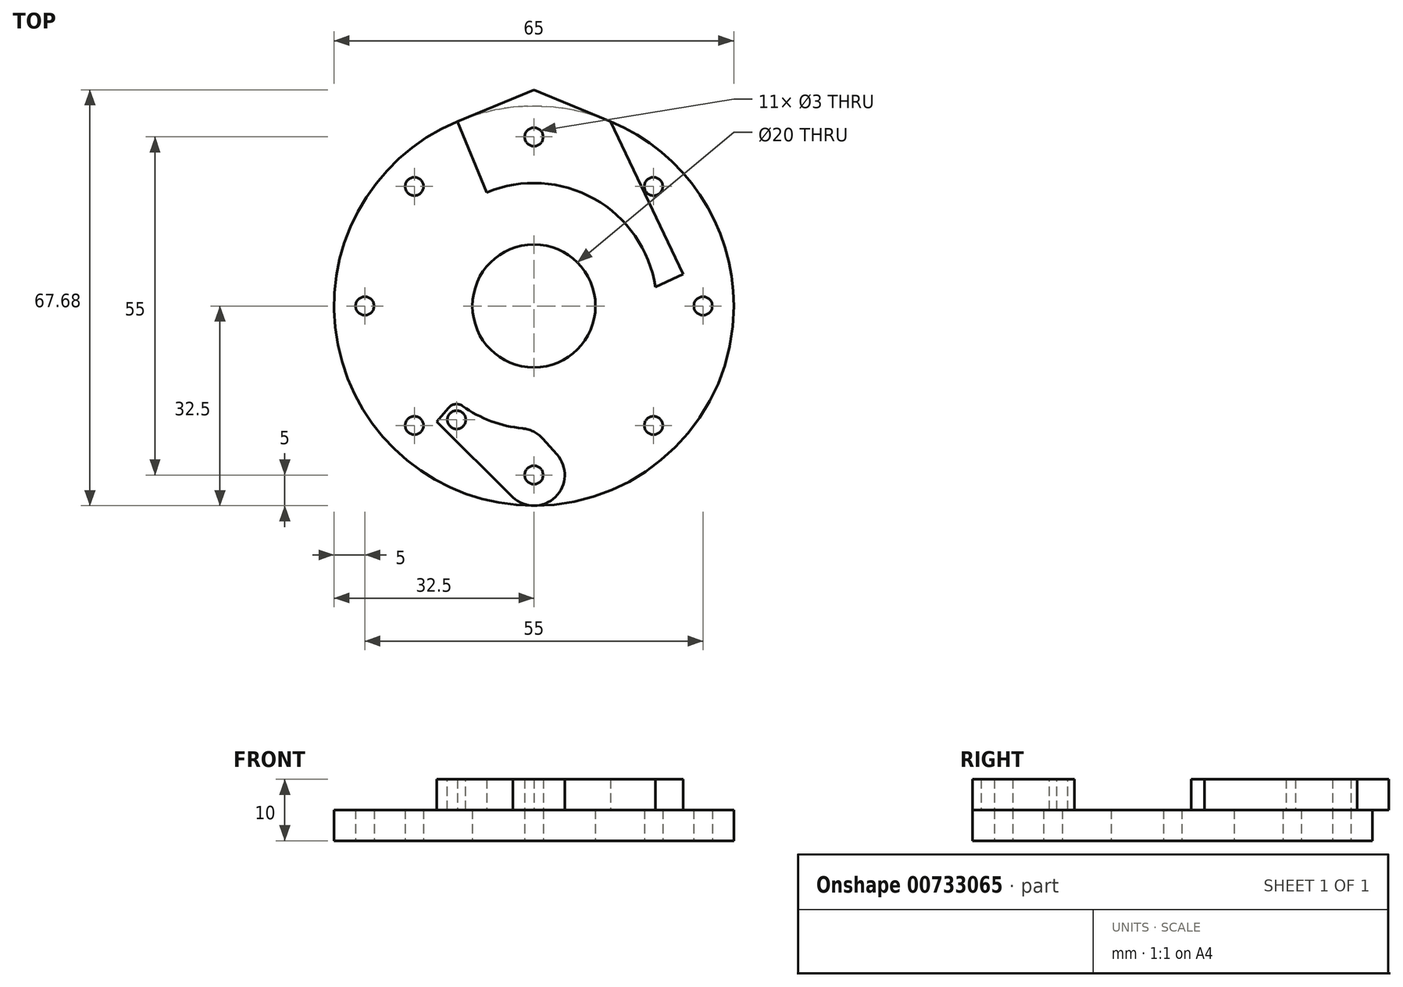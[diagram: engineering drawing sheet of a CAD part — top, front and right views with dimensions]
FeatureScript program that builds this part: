
annotation { "Feature Type Name" : "Feature", "Feature Type Description" : "" }
export const myFeature = defineFeature(function(context is Context, id is Id, definition is map)
    precondition{}
    {
        {
            var Q0;
            Q0=qCreatedBy(makeId("Top.planeOp"),FACE);
            var sketch = newSketch(context, id + "F0", { "sketchPlane" : qUnion([Q0])});
            skCircle(sketch, "E0", {"center": v(0, 0) * mm, "radius": 32.5 * mm});
            skCircle(sketch, "E1", {"center": v(0, 27.5) * mm, "radius": 1.5 * mm});
            skPoint(sketch, "E2", {"position": v(0, 32.5) * mm});
            skCircle(sketch, "E3.1.0", {"center": v(-19.45, 19.45) * mm, "radius": 1.5 * mm});
            skCircle(sketch, "E3.2.0", {"center": v(-27.5, 0) * mm, "radius": 1.5 * mm});
            skCircle(sketch, "E3.3.0", {"center": v(-19.45, -19.45) * mm, "radius": 1.5 * mm});
            skCircle(sketch, "E3.4.0", {"center": v(0, -27.5) * mm, "radius": 1.5 * mm});
            skCircle(sketch, "E3.5.0", {"center": v(19.45, -19.45) * mm, "radius": 1.5 * mm});
            skCircle(sketch, "E3.6.0", {"center": v(27.5, 0) * mm, "radius": 1.5 * mm});
            skCircle(sketch, "E3.7.0", {"center": v(19.45, 19.45) * mm, "radius": 1.5 * mm});
            skCircle(sketch, "E4", {"center": v(0, 0) * mm, "radius": 10 * mm});
            skSolve(sketch);
        }
        {
            var Q0;
            Q0=qSketchRegion(id+"F0",true);
            extrude(context, id + "F1", {"entities" : qUnion([Q0]), "depth" : 5 * mm, "offsetDistance" : 25 * mm});
        }
        {
            var Q0;
            Q0=makeQuery(id+"F1.opExtrude","CAP_FACE",FACE,{"disambiguationData":[OSD([sQuery(id+"F0.wireOp",EDGE,"E0"),sQuery(id+"F0.wireOp",EDGE,"E1"),sQuery(id+"F0.wireOp",EDGE,"E3.1.0"),sQuery(id+"F0.wireOp",EDGE,"E3.2.0"),sQuery(id+"F0.wireOp",EDGE,"E3.3.0"),sQuery(id+"F0.wireOp",EDGE,"E3.4.0"),sQuery(id+"F0.wireOp",EDGE,"E3.5.0"),sQuery(id+"F0.wireOp",EDGE,"E3.6.0"),sQuery(id+"F0.wireOp",EDGE,"E3.7.0")])],"isStart":false});
            var sketch = newSketch(context, id + "F2", { "sketchPlane" : qUnion([Q0])});
            skCircle(sketch, "E5.0", {"center": v(0, 0) * mm, "radius": 32.5 * mm, "construction": true});
            skLineSegment(sketch, "E6.0", {"start": v(0, 35.18) * mm, "end": v(24.87, 24.87) * mm});
            skLineSegment(sketch, "E6.1", {"start": v(24.87, 24.87) * mm, "end": v(35.18, 0) * mm});
            skLineSegment(sketch, "E6.2", {"start": v(35.18, 0) * mm, "end": v(24.87, -24.87) * mm});
            skLineSegment(sketch, "E6.3", {"start": v(24.87, -24.87) * mm, "end": v(0, -35.18) * mm});
            skLineSegment(sketch, "E6.4", {"start": v(0, -35.18) * mm, "end": v(-24.87, -24.87) * mm});
            skLineSegment(sketch, "E6.5", {"start": v(-24.87, -24.87) * mm, "end": v(-35.18, 0) * mm});
            skLineSegment(sketch, "E6.6", {"start": v(-35.18, 0) * mm, "end": v(-24.87, 24.87) * mm});
            skLineSegment(sketch, "E6.7", {"start": v(-24.87, 24.87) * mm, "end": v(0, 35.18) * mm});
            skPoint(sketch, "E6.0.midPoint", {"position": v(12.44, 30.03) * mm});
            skCircle(sketch, "E7", {"center": v(0, 0) * mm, "radius": 20 * mm});
            skPoint(sketch, "E8", {"position": v(-12.44, 30.03) * mm});
            skLineSegment(sketch, "E9", {"start": v(-12.44, 30.03) * mm, "end": v(-7.65, 18.48) * mm});
            skLineSegment(sketch, "E10.MirrorCS", {"start": v(12.44, 30.03) * mm, "end": v(7.65, 18.48) * mm, "construction": true});
            skCircle(sketch, "E11.0", {"center": v(0, 27.5) * mm, "radius": 1.5 * mm});
            skLineSegment(sketch, "E12", {"start": v(12.44, 30.03) * mm, "end": v(24.28, 5.2) * mm});
            skLineSegment(sketch, "E13", {"start": v(24.28, 5.2) * mm, "end": v(19.77, 3.05) * mm});
            skArc(sketch, "E14.trimOffspring", {"start": v(-16.07, -19.15) * mm, "mid": v(-10.46, -22.7) * mm, "end": v(-4.11, -24.66) * mm});
            skLineSegment(sketch, "E15", {"start": v(-16.07, -19.15) * mm, "end": v(-12.86, -15.32) * mm});
            skCircle(sketch, "E16", {"center": v(0, -27.5) * mm, "radius": 5 * mm});
            skLineSegment(sketch, "E17", {"start": v(0, -22.5) * mm, "end": v(0, -20) * mm});
            skLineSegment(sketch, "E18", {"start": v(-17.16, -18.18) * mm, "end": v(-3.43, -31.14) * mm});
            skLineSegment(sketch, "E19", {"start": v(0, -20) * mm, "end": v(3.73, -24.17) * mm});
            skLineSegment(sketch, "E20", {"start": v(-16.07, -19.15) * mm, "end": v(-16.1, -19.18) * mm});
            skSolve(sketch);
        }
        {
            var Q0;
            Q0=makeQuery(id+"F2.imprint","IMPRINT",FACE,{"disambiguationData":[TD([[makeQuery(id+"F2.imprint","IMPRINT",EDGE,{"derivedFrom":makeQuery(id+"F1.opExtrude","CAP_EDGE",EDGE,{"disambiguationData":[OSD([sQuery(id+"F0.wireOp",EDGE,"E3.4.0")])],"isStart":false})}),-1.0]])]});
            var Q1;
            {var subQ0=sQuery(id+"F2.wireOp",EDGE,"E15");var subQ1=sQuery(id+"F2.wireOp",EDGE,"E14.trimOffspring");var subQ2=makeQuery(id+"F2.imprint","INTERSECT",VERTEX,{"derivedFrom":[subQ1,subQ0]});Q1=makeQuery(id+"F2.imprint","IMPRINT",FACE,{"disambiguationData":[TD([[makeQuery(id+"F2.imprint","IMPRINT",EDGE,{"disambiguationData":[TD([[subQ2,-1.0]])],"derivedFrom":subQ1}),1.0]])]});}
            var Q2;
            {var subQ0=sQuery(id+"F2.wireOp",EDGE,"E14.trimOffspring");var subQ1=makeQuery(id+"F1.opExtrude","CAP_EDGE",EDGE,{"disambiguationData":[OSD([sQuery(id+"F0.wireOp",EDGE,"E3.3.0")])],"isStart":false});var subQ2=makeQuery(id+"F2.imprint","INTERSECT",VERTEX,{"disambiguationData":[OD(0.0)],"derivedFrom":[subQ1,subQ0]});Q2=makeQuery(id+"F2.imprint","IMPRINT",FACE,{"disambiguationData":[TD([[makeQuery(id+"F2.imprint","IMPRINT",EDGE,{"disambiguationData":[TD([[subQ2,-1.0]])],"derivedFrom":subQ0}),1.0]])]});}
            var Q3;
            {var subQ3=sQuery(id+"F2.wireOp",EDGE,"TiWqFANf-cDh7-nF8t-lKnd-fGeFsKGwED6M");Q3=makeQuery(id+"F2.imprint","IMPRINT",FACE,{"disambiguationData":[TD([[makeQuery(id+"F2.imprint","IMPRINT",EDGE,{"derivedFrom":subQ3}),1.0]])]});}
            var Q4;
            {var subQ6=sQuery(id+"F2.wireOp",EDGE,"E9");Q4=makeQuery(id+"F2.imprint","IMPRINT",FACE,{"disambiguationData":[TD([[makeQuery(id+"F2.imprint","IMPRINT",EDGE,{"derivedFrom":subQ6}),1.0]])]});}
            var Q5;
            {var subQ0=sQuery(id+"F2.wireOp",EDGE,"E12");var subQ1=makeQuery(id+"F1.opExtrude","CAP_EDGE",EDGE,{"disambiguationData":[OSD([sQuery(id+"F0.wireOp",EDGE,"E3.7.0")])],"isStart":false});var subQ2=makeQuery(id+"F2.imprint","INTERSECT",VERTEX,{"disambiguationData":[OD(0.0)],"derivedFrom":[subQ1,subQ0]});Q5=makeQuery(id+"F2.imprint","IMPRINT",FACE,{"disambiguationData":[TD([[makeQuery(id+"F2.imprint","IMPRINT",EDGE,{"disambiguationData":[TD([[subQ2,-1.0]])],"derivedFrom":subQ0}),-1.0]])]});}
            var Q6;
            {var subQ0=sQuery(id+"F2.wireOp",EDGE,"E6.7");var subQ1=sQuery(id+"F2.wireOp",EDGE,"E6.0");var subQ2=makeQuery(id+"F2.imprint","INTERSECT",VERTEX,{"derivedFrom":[subQ1,subQ0]});Q6=makeQuery(id+"F2.imprint","IMPRINT",FACE,{"disambiguationData":[TD([[makeQuery(id+"F2.imprint","IMPRINT",EDGE,{"disambiguationData":[TD([[subQ2,-1.0]])],"derivedFrom":subQ1}),-1.0]])]});}
            var Q7;
            {var subQ0=sQuery(id+"F2.wireOp",EDGE,"E17");Q7=makeQuery(id+"F2.imprint","IMPRINT",FACE,{"disambiguationData":[TD([[makeQuery(id+"F2.imprint","IMPRINT",EDGE,{"derivedFrom":subQ0}),-1.0]])]});}
            var Q8;
            {var subQ3=sQuery(id+"F2.wireOp",EDGE,"E18");Q8=makeQuery(id+"F2.imprint","IMPRINT",FACE,{"disambiguationData":[TD([[makeQuery(id+"F2.imprint","IMPRINT",EDGE,{"derivedFrom":subQ3}),1.0]])]});}
            extrude(context, id + "F3", {"entities" : qUnion([Q0, Q1, Q2, Q3, Q4, Q5, Q6, Q7, Q8]), "depth" : 5 * mm, "offsetDistance" : 25 * mm});
        }
        {
            var Q0;
            Q0=makeQuery(id+"F3.opExtrude","CAP_FACE",FACE,{"disambiguationData":[OSD([sQuery(id+"F0.wireOp",EDGE,"E3.4.0"),sQuery(id+"F2.wireOp",EDGE,"E7"),sQuery(id+"F2.wireOp",EDGE,"E15"),sQuery(id+"F2.wireOp",EDGE,"E16"),sQuery(id+"F2.wireOp",EDGE,"E18"),sQuery(id+"F2.wireOp",EDGE,"E19"),sQuery(id+"F2.wireOp",EDGE,"E20")])],"isStart":false});
            var sketch = newSketch(context, id + "F4", { "sketchPlane" : qUnion([Q0])});
            skLineSegment(sketch, "E21", {"start": v(-15.78, -18.8) * mm, "end": v(-3.43, -31.14) * mm});
            skLineSegment(sketch, "E22", {"start": v(-15.78, -18.8) * mm, "end": v(-12.3, -21.72) * mm, "construction": true});
            skLineSegment(sketch, "E23", {"start": v(-12.86, -15.32) * mm, "end": v(-9.38, -18.24) * mm, "construction": true});
            skLineSegment(sketch, "E24", {"start": v(-12.3, -21.72) * mm, "end": v(-9.38, -18.24) * mm, "construction": true});
            skLineSegment(sketch, "E25", {"start": v(-10.84, -19.98) * mm, "end": v(-14.32, -17.06) * mm, "construction": true});
            skCircle(sketch, "E26", {"center": v(-12.58, -18.52) * mm, "radius": 1.5 * mm});
            skSolve(sketch);
        }
        {
            var Q0;
            {var subQ0=sQuery(id+"F4.wireOp",EDGE,"E21");Q0=makeQuery(id+"F4.imprint","IMPRINT",FACE,{"disambiguationData":[TD([[makeQuery(id+"F4.imprint","IMPRINT",EDGE,{"derivedFrom":subQ0}),-1.0]])]});}
            var Q1;
            Q1=makeQuery(id+"F4.imprint","IMPRINT",FACE,{"disambiguationData":[TD([[makeQuery(id+"F4.imprint","IMPRINT",EDGE,{"derivedFrom":sQuery(id+"F4.wireOp",EDGE,"E26")}),1.0]])]});
            extrude(context, id + "F5", {"entities" : qUnion([Q0, Q1]), "operationType" : NewBodyOperationType.REMOVE, "endBound" : BoundingType.UP_TO_NEXT, "oppositeDirection" : true, "depth" : 25 * mm, "offsetDistance" : 25 * mm});
        }
        {
            var Q0;
            Q0=makeQuery(id+"F5.boolean.opBoolean","COPY",EDGE,{"derivedFrom":makeQuery(id+"F5.opExtrude","SWEPT_EDGE",EDGE,{"disambiguationData":[OSD([sQuery(id+"F2.wireOp",EDGE,"E15"),sQuery(id+"F2.wireOp",EDGE,"E20"),sQuery(id+"F4.wireOp",EDGE,"E21")])]})});
            var Q1;
            Q1=makeQuery(id+"F3.opExtrude","SWEPT_EDGE",EDGE,{"disambiguationData":[OSD([sQuery(id+"F2.wireOp",EDGE,"E7"),sQuery(id+"F2.wireOp",EDGE,"E15")])]});
            fillet(context, id + "F6", {"entities" : qUnion([Q0, Q1]), "radius" : 1.7 * mm, "tangentPropagation" : true, "allowEdgeOverflow" : false});
        }
        {
            var Q0;
            Q0=makeQuery(id+"F3.opExtrude","SWEPT_EDGE",EDGE,{"disambiguationData":[OSD([sQuery(id+"F2.wireOp",EDGE,"E7"),sQuery(id+"F2.wireOp",EDGE,"E17"),sQuery(id+"F2.wireOp",EDGE,"E19")])]});
            fillet(context, id + "F7", {"entities" : qUnion([Q0]), "radius" : 5 * mm, "tangentPropagation" : true, "allowEdgeOverflow" : false});
        }
    });
